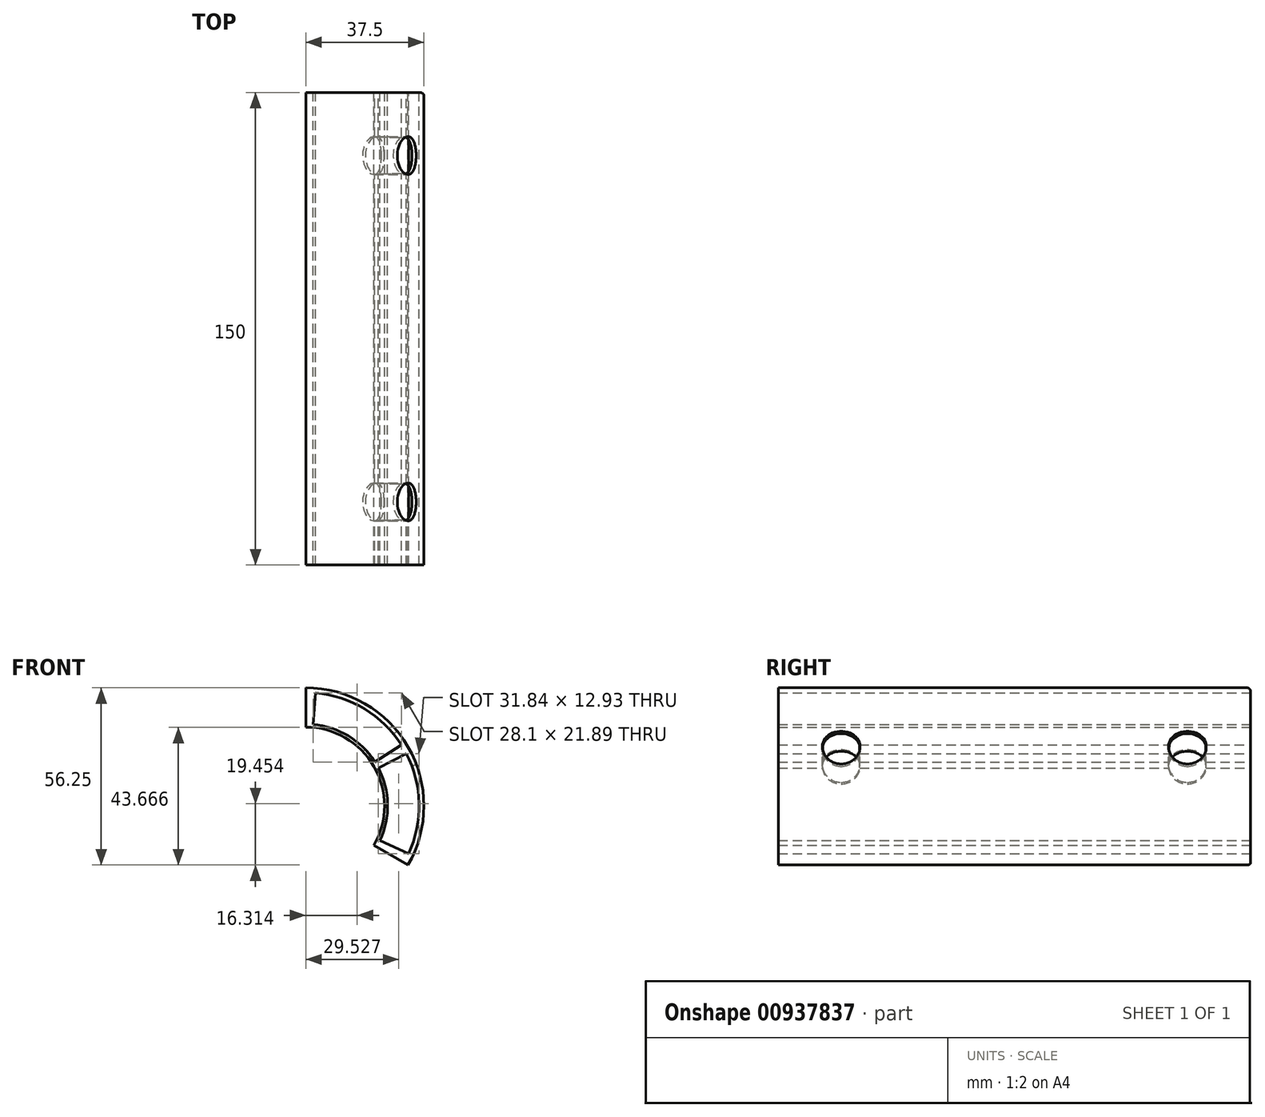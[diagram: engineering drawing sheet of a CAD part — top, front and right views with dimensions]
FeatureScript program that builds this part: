
annotation { "Feature Type Name" : "Feature", "Feature Type Description" : "" }
export const myFeature = defineFeature(function(context is Context, id is Id, definition is map)
    precondition{}
    {
        {
            var Q0;
            Q0=qCreatedBy(makeId("Front.planeOp"),FACE);
            var sketch = newSketch(context, id + "F0", { "sketchPlane" : qUnion([Q0])});
            skCircle(sketch, "E0", {"center": v(0, 0) * mm, "radius": 37.5 * mm});
            skCircle(sketch, "E1", {"center": v(0, 0) * mm, "radius": 25 * mm});
            skLineSegment(sketch, "E2", {"start": v(0, 0) * mm, "end": v(0, 37.5) * mm});
            skLineSegment(sketch, "E3", {"start": v(0, 0) * mm, "end": v(32.48, -18.75) * mm});
            skLineSegment(sketch, "E4", {"start": v(0, 0) * mm, "end": v(32.48, 18.75) * mm});
            skSolve(sketch);
        }
        {
            var Q0;
            {var subQ0=sQuery(id+"F0.wireOp",EDGE,"E2");var subQ1=sQuery(id+"F0.wireOp",EDGE,"E0");var subQ2=makeQuery(id+"F0.imprint","INTERSECT",VERTEX,{"derivedFrom":[subQ1,subQ0]});Q0=makeQuery(id+"F0.imprint","IMPRINT",FACE,{"disambiguationData":[TD([[makeQuery(id+"F0.imprint","IMPRINT",EDGE,{"disambiguationData":[TD([[subQ2,1.0]])],"derivedFrom":subQ1}),1.0]])]});}
            var Q1;
            {var subQ0=sQuery(id+"F0.wireOp",EDGE,"E3");var subQ1=sQuery(id+"F0.wireOp",EDGE,"E0");var subQ2=makeQuery(id+"F0.imprint","INTERSECT",VERTEX,{"derivedFrom":[subQ1,subQ0]});Q1=makeQuery(id+"F0.imprint","IMPRINT",FACE,{"disambiguationData":[TD([[makeQuery(id+"F0.imprint","IMPRINT",EDGE,{"disambiguationData":[TD([[subQ2,-1.0]])],"derivedFrom":subQ1}),1.0]])]});}
            extrude(context, id + "F1", {"entities" : qUnion([Q0, Q1]), "depth" : 150 * mm, "offsetDistance" : 25 * mm, "symmetric" : true});
        }
        {
            var Q0;
            Q0=sQuery(id+"F0.wireOp",VERTEX,"E4.end");
            var Q1;
            Q1=sQuery(id+"F0.wireOp",VERTEX,"E2.start");
            cPlane(context, id + "F2", {"entities" : qUnion([Q0, Q1]), "cplaneType" : CPlaneType.MID_PLANE, "offset" : 25 * mm, "width" : 150 * mm, "height" : 150 * mm});
        }
        {
            var Q0;
            Q0=qCreatedBy(id+"F2.planeOp",FACE);
            cPlane(context, id + "F3", {"entities" : qUnion([Q0]), "cplaneType" : CPlaneType.OFFSET, "offset" : 20 * mm, "oppositeDirection" : true, "width" : 150 * mm, "height" : 150 * mm});
        }
        {
            var Q0;
            Q0=qCreatedBy(id+"F3.planeOp",FACE);
            var sketch = newSketch(context, id + "F4", { "sketchPlane" : qUnion([Q0])});
            skLineSegment(sketch, "E5", {"start": v(0, 0) * mm, "end": v(-75, 0) * mm});
            skLineSegment(sketch, "E6", {"start": v(-75, 0) * mm, "end": v(0, 0) * mm});
            skLineSegment(sketch, "E7", {"start": v(75, 0) * mm, "end": v(0, 0) * mm});
            skPoint(sketch, "E8", {"position": v(-55, 0) * mm});
            skPoint(sketch, "E9", {"position": v(55, 0) * mm});
            skSolve(sketch);
        }
        {
            var Q0;
            Q0=sQuery(id+"F4.wireOp",VERTEX,"E9");
            var Q1;
            Q1=sQuery(id+"F4.wireOp",VERTEX,"E8");
            var Q2;
            Q2=makeQuery(id+"F1.opExtrude","SWEPT_BODY",BODY,{"disambiguationData":[OSD([sQuery(id+"F0.wireOp",EDGE,"E0"),sQuery(id+"F0.wireOp",EDGE,"E1"),sQuery(id+"F0.wireOp",EDGE,"E2"),sQuery(id+"F0.wireOp",EDGE,"E3")])]});
            hole(context, id + "F5", {"style" : HoleStyle.SIMPLE, "endStyle" : HoleEndStyle.THROUGH, "oppositeDirection" : true, "holeDiameter" : 12 * mm, "majorDiameter" : 5 * mm, "isTappedThrough" : true, "tappedDepth" : 12 * mm, "tapClearance" : 3, "locations" : qUnion([Q0, Q1]), "scope" : qUnion([Q2])});
        }
        {
            var Q0;
            Q0=makeQuery(id+"F1.opExtrude","CAP_FACE",FACE,{"disambiguationData":[OSD([sQuery(id+"F0.wireOp",EDGE,"E0"),sQuery(id+"F0.wireOp",EDGE,"E1"),sQuery(id+"F0.wireOp",EDGE,"E2"),sQuery(id+"F0.wireOp",EDGE,"E3")])],"isStart":true});
            var sketch = newSketch(context, id + "F6", { "sketchPlane" : qUnion([Q0])});
            skCircle(sketch, "E10", {"center": v(0, 0) * mm, "radius": 26 * mm});
            skCircle(sketch, "E11", {"center": v(0, 0) * mm, "radius": 36 * mm});
            skLineSegment(sketch, "E12", {"start": v(-30.36, 19.34) * mm, "end": v(-21.93, 13.97) * mm});
            skLineSegment(sketch, "E13", {"start": v(-3.14, 35.86) * mm, "end": v(-2.27, 25.9) * mm});
            skLineSegment(sketch, "E14", {"start": v(-31.93, 16.62) * mm, "end": v(-23.06, 12) * mm});
            skLineSegment(sketch, "E15", {"start": v(-32.63, -15.21) * mm, "end": v(-23.56, -10.99) * mm});
            skLineSegment(sketch, "E16", {"start": v(-3.14, 35.86) * mm, "end": v(0, 0) * mm});
            skLineSegment(sketch, "E17", {"start": v(-30.36, 19.34) * mm, "end": v(0, 0) * mm});
            skLineSegment(sketch, "E18", {"start": v(-31.93, 16.62) * mm, "end": v(0, 0) * mm});
            skLineSegment(sketch, "E19", {"start": v(-32.63, -15.21) * mm, "end": v(0, 0) * mm});
            skSolve(sketch);
        }
        {
            var Q0;
            {var subQ0=sQuery(id+"F6.wireOp",EDGE,"E16");var subQ1=sQuery(id+"F6.wireOp",EDGE,"E10");var subQ2=makeQuery(id+"F6.imprint","INTERSECT",VERTEX,{"derivedFrom":[subQ1,subQ0]});Q0=makeQuery(id+"F6.imprint","IMPRINT",FACE,{"disambiguationData":[TD([[makeQuery(id+"F6.imprint","IMPRINT",EDGE,{"disambiguationData":[TD([[subQ2,-1.0]])],"derivedFrom":subQ1}),-1.0]])]});}
            var Q1;
            {var subQ0=sQuery(id+"F6.wireOp",EDGE,"E18");var subQ1=sQuery(id+"F6.wireOp",EDGE,"E10");var subQ2=makeQuery(id+"F6.imprint","INTERSECT",VERTEX,{"derivedFrom":[subQ1,subQ0]});Q1=makeQuery(id+"F6.imprint","IMPRINT",FACE,{"disambiguationData":[TD([[makeQuery(id+"F6.imprint","IMPRINT",EDGE,{"disambiguationData":[TD([[subQ2,-1.0]])],"derivedFrom":subQ1}),-1.0]])]});}
            extrude(context, id + "F7", {"entities" : qUnion([Q0, Q1]), "operationType" : NewBodyOperationType.REMOVE, "oppositeDirection" : true, "depth" : 150 * mm, "offsetDistance" : 25 * mm});
        }
        {
            var Q0;
            Q0=makeQuery(id+"F1.opExtrude","CAP_EDGE",EDGE,{"disambiguationData":[OSD([sQuery(id+"F0.wireOp",EDGE,"E0")])],"isStart":true});
            fillet(context, id + "F8", {"entities" : qUnion([Q0]), "radius" : 1 * mm, "tangentPropagation" : true, "allowEdgeOverflow" : false});
        }
    });
